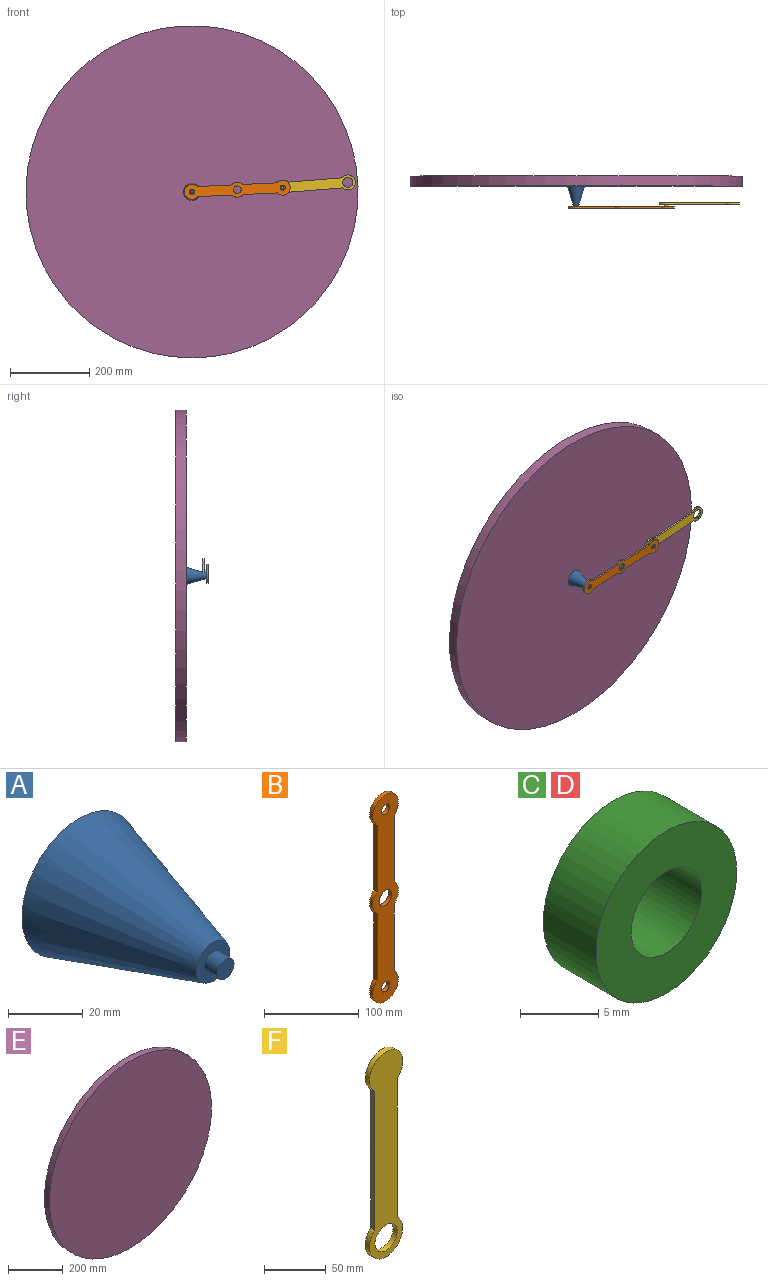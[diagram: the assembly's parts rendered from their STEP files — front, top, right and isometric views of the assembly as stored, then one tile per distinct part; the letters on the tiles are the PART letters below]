
ASSEMBLY  parts=6 mates=5
PART A: 5 faces, bbox 43.2x55.6x43.2 mm
  f0: plane 12.7x12.7mm, normal (0,-1,0), area 95mm2, adj f2,f4
  f1: plane 43.18x43.18mm, normal (0,1,0), area 1464.4mm2, adj f4
  f2: cylinder r=3.17mm len=6.35mm, axis (0,1,0), area 95mm2, adj f0,f3
  f3: plane 6.35x6.35mm, normal (0,-1,0), area 31.7mm2, adj f2
  f4: cone r=6.35mm half-angle=16.7deg, axis (0,1,0), area 4655.4mm2, adj f0,f1
PART B: 13 faces, bbox 38.1x4.8x266.9 mm
  f0: plane 85.9x4.76mm, normal (1,0,0), area 409.1mm2, adj f1,f9,f11,f12
  f1: cylinder r=19.05mm len=38.1mm, axis (0,1,0), area 437.6mm2, adj f0,f2,f11,f12
  f2: plane 85.9x4.76mm, normal (-1,0,0), area 409.1mm2, adj f1,f3,f11,f12
  f3: cylinder r=19.05mm len=28.4mm, axis (0,1,0), area 152.6mm2, adj f2,f4,f11,f12
  f4: plane 86.15x4.76mm, normal (-1,0,0), area 410.3mm2, adj f3,f5,f11,f12
  f5: cylinder r=19.05mm len=38.1mm, axis (0,1,0), area 437.6mm2, adj f4,f6,f11,f12
  f6: plane 86.15x4.76mm, normal (1,0,0), area 410.3mm2, adj f5,f9,f11,f12
  f7: cylinder r=9.53mm len=19.05mm, axis (0,1,0), area 285mm2, adj f11,f12
  f8: cylinder r=6.35mm len=12.7mm, axis (0,1,0), area 190mm2, adj f11,f12
  f9: cylinder r=19.05mm len=28.4mm, axis (0,1,0), area 152.6mm2, adj f0,f6,f11,f12
  f10: cylinder r=6.35mm len=12.7mm, axis (0,1,0), area 190mm2, adj f11,f12
  f11: plane 266.95x38.1mm, normal (0,-1,0), area 6914mm2, adj f0,f1,f2,f3,f4,f5,f6,f7
  f12: plane 266.95x38.1mm, normal (0,1,0), area 6914mm2, adj f0,f1,f2,f3,f4,f5,f6,f7
PART C: 4 faces, bbox 12.7x4.8x12.7 mm
  f0: cylinder r=3.17mm len=6.35mm, axis (0,1,0), area 95mm2, adj f2,f3
  f1: cylinder r=6.35mm len=12.7mm, axis (0,1,0), area 190mm2, adj f2,f3
  f2: plane 12.7x12.7mm, normal (0,-1,0), area 95mm2, adj f0,f1
  f3: plane 12.7x12.7mm, normal (0,1,0), area 95mm2, adj f0,f1
PART D: same geometry as C
PART E: 3 faces, bbox 838.2x25.4x838.2 mm
  f0: cylinder r=419.1mm len=838.2mm, axis (0,1,0), area 66885.4mm2, adj f1,f2
  f1: plane 838.2x838.2mm, normal (0,-1,0), area 551804.4mm2, adj f0
  f2: plane 838.2x838.2mm, normal (0,1,0), area 551804.4mm2, adj f0
PART F: 13 faces, bbox 38.1x14.3x203.3 mm
  f0: plane 136.79x4.76mm, normal (1,0,0), area 651.5mm2, adj f1,f3,f5,f6
  f1: cylinder r=19.05mm len=38.1mm, axis (0,1,0), area 437.6mm2, adj f0,f2,f5,f6
  f2: plane 136.79x4.76mm, normal (-1,0,0), area 651.5mm2, adj f1,f3,f5,f6
  f3: cylinder r=19.05mm len=38.1mm, axis (0,1,0), area 437.6mm2, adj f0,f2,f5,f6
  f4: cylinder r=12.7mm len=25.4mm, axis (0,1,0), area 380mm2, adj f5,f6
  f5: plane 203.29x38.1mm, normal (0,-1,0), area 5079mm2, adj f0,f1,f2,f3,f4
  f6: plane 203.29x38.1mm, normal (0,1,0), area 4952.3mm2, adj f0,f1,f2,f3,f4,f7,f8
  f7: cylinder r=6.35mm len=12.7mm, axis (0,-1,0), area 95mm2, adj f6,f8,f9
  f8: extruded ~12.7x6.35mm, area 95mm2, adj f6,f7,f9
  f9: plane 14.61x12.7mm, normal (0,1,0), area 95mm2, adj f7,f8,f11,f12
  f10: plane 7.3x6.35mm, normal (0,1,0), area 31.7mm2, adj f11,f12
  f11: cylinder r=3.17mm len=6.35mm, axis (0,-1,0), area 47.5mm2, adj f9,f10,f12
  f12: extruded ~6.35x4.76mm, area 47.5mm2, adj f9,f10,f11
PLACE A t=(0.81,10.78,0.77)mm
PLACE B rot(axis=(0,1,0),87.3deg) t=(229.41,-40.02,11.38)mm
PLACE C t=(0.81,-40.02,0.77)mm
PLACE D t=(229.41,-40.02,11.38)mm
PLACE E t=(0.81,36.18,0.77)mm
PLACE F rot(axis=(0.73,0,-0.68),180deg) t=(229.41,-35.26,11.38)mm
MATE revolute B.f10 <-> C.f1  axis (0,-1,0) through (0.81,-44.78,0.77)mm
MATE revolute D.f0 <-> B.f8  axis (0,-1,0) through (229.41,-44.78,11.38)mm
MATE revolute F.f11 <-> B.f8  axis (0,-1,0) through (229.41,-44.78,11.38)mm
MATE fastened E.f0 <-> A.f4  axis (0,-1,0) through (0.81,10.78,0.77)mm
MATE revolute C.f0 <-> A.f2  axis (0,-1,0) through (0.81,-44.78,0.77)mm
